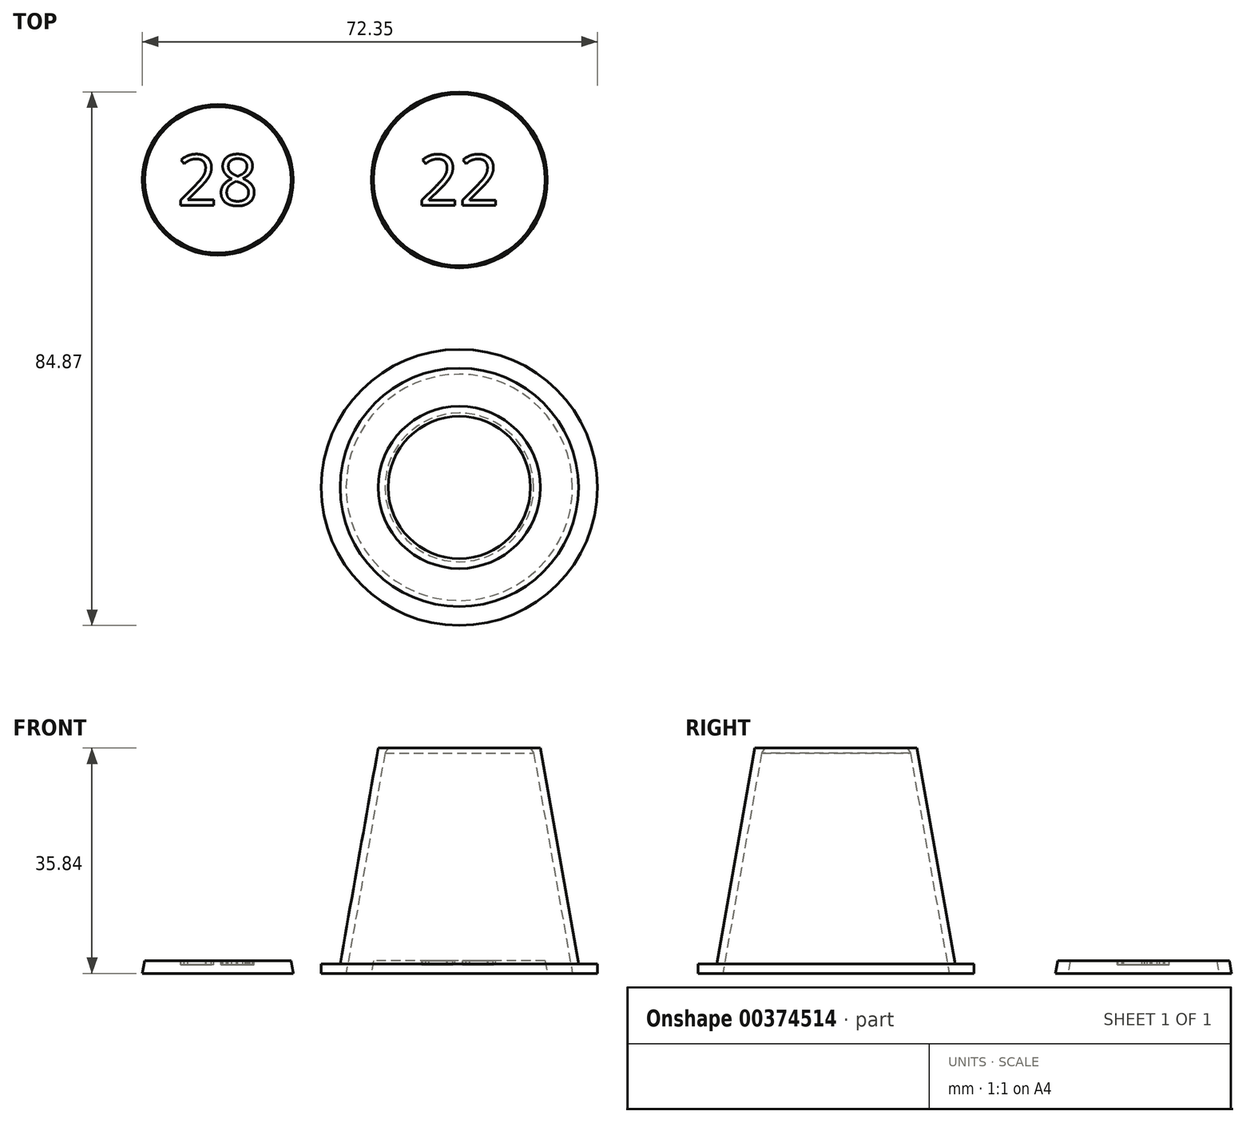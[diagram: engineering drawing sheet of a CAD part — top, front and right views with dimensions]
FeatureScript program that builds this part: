
annotation { "Feature Type Name" : "Feature", "Feature Type Description" : "" }
export const myFeature = defineFeature(function(context is Context, id is Id, definition is map)
    precondition{}
    {
        {
            var Q0;
            Q0=qCreatedBy(makeId("Front.planeOp"),FACE);
            var sketch = newSketch(context, id + "F0", { "sketchPlane" : qUnion([Q0])});
            skLineSegment(sketch, "E0", {"start": v(0, 0) * mm, "end": v(0, 35) * mm, "construction": true});
            skLineSegment(sketch, "E1", {"start": v(-11.83, 35) * mm, "end": v(-18, 0) * mm});
            skLineSegment(sketch, "E2", {"start": v(-18, 0) * mm, "end": v(0, 0) * mm, "construction": true});
            skLineSegment(sketch, "E3", {"start": v(0, 35) * mm, "end": v(-11.83, 35) * mm, "construction": true});
            skLineSegment(sketch, "E4.0", {"start": v(-12.9, 35.84) * mm, "end": v(-18.95, 1.5) * mm});
            skLineSegment(sketch, "E5", {"start": v(-18, 0) * mm, "end": v(-21.95, 0) * mm});
            skLineSegment(sketch, "E6", {"start": v(-21.95, 0) * mm, "end": v(-21.95, 1.5) * mm});
            skLineSegment(sketch, "E7", {"start": v(-21.95, 1.5) * mm, "end": v(-18.95, 1.5) * mm});
            skPoint(sketch, "E8.orphan", {"position": v(-18, 1.5) * mm});
            skLineSegment(sketch, "E9", {"start": v(-11.83, 35) * mm, "end": v(-11.32, 35.84) * mm});
            skLineSegment(sketch, "E10", {"start": v(-11.32, 35.84) * mm, "end": v(-12.9, 35.84) * mm});
            skSolve(sketch);
        }
        {
            var Q0;
            Q0 = qSketchRegion(id + "F0", true);
            var Q1;
            Q1=sQuery(id+"F0.wireOp",EDGE,"E0");
            revolve(context, id + "F1", {"entities" : qUnion([Q0]), "axis" : qUnion([Q1]), "revolveType" : RevolveType.FULL});
        }
        {
            var Q0;
            Q0=qCreatedBy(makeId("Top.planeOp"),FACE);
            var sketch = newSketch(context, id + "F2", { "sketchPlane" : qUnion([Q0])});
            skCircle(sketch, "E11", {"center": v(0, 48.92) * mm, "radius": 14 * mm});
            skCircle(sketch, "E12", {"center": v(-38.4, 48.92) * mm, "radius": 12 * mm});
            skSolve(sketch);
        }
        {
            var Q0;
            Q0 = qSketchRegion(id + "F2", true);
            extrude(context, id + "F3", {"entities" : qUnion([Q0]), "depth" : 2 * mm, "hasDraft" : true, "draftAngle" : 10 * degree, "draftPullDirection" : true});
        }
        {
            var Q0;
            Q0=makeQuery(id+"F3.opExtrude","CAP_FACE",FACE,{"disambiguationData":[OSD([sQuery(id+"F2.wireOp",EDGE,"E12")])],"isStart":false});
            var sketch = newSketch(context, id + "F4", { "sketchPlane" : qUnion([Q0])});
            skText(sketch, "E13", { "text": "28", "fontName": "OpenSans-Regular.ttf"});
            skLineSegment(sketch, "E14", {"start": v(-38.4, 48.92) * mm, "end": v(-44.9, 48.92) * mm, "construction": true});
            skLineSegment(sketch, "E15", {"start": v(-45.15, 58.41) * mm, "end": v(-38.4, 48.92) * mm, "construction": true});
            const initialGuessF4  = {"E13": [-0.0449, 0.04488, 1, 0, 0.0081]};
            skSetInitialGuess(sketch, initialGuessF4);
            skSolve(sketch);
        }
        {
            var Q0;
            Q0=makeQuery(id+"F3.opExtrude","CAP_FACE",FACE,{"disambiguationData":[OSD([sQuery(id+"F2.wireOp",EDGE,"E11")])],"isStart":false});
            var sketch = newSketch(context, id + "F5", { "sketchPlane" : qUnion([Q0])});
            skText(sketch, "E16", { "text": "22", "fontName": "OpenSans-Regular.ttf"});
            skLineSegment(sketch, "E17", {"start": v(-10.98, 57.03) * mm, "end": v(0, 48.92) * mm, "construction": true});
            const initialGuessF5  = {"E16": [-0.0065, 0.04487, 1, 0, 0.0081]};
            skSetInitialGuess(sketch, initialGuessF5);
            skSolve(sketch);
        }
        {
            var Q0;
            Q0 = qSketchRegion(id + "F4", true);
            var Q1;
            Q1 = qSketchRegion(id + "F5", true);
            extrude(context, id + "F6", {"entities" : qUnion([Q0, Q1]), "operationType" : NewBodyOperationType.REMOVE, "oppositeDirection" : true, "depth" : 0.6 * mm});
        }
    });
